# Revit family: UL1008BCELTS1277
name_source: partatom
category: Communication Devices
units: mm (PartAtom-declared; Revit-internal decimal feet)

## family parameters
Cut with Voids When Loaded = No
Host = Face
Maintain Annotation Orientation = No
OmniClass Number = 23.85.80.11.27
OmniClass Title = Lighting Controls
Part Type = Normal
Room Calculation Point = No
Round Connector Dimension = Use Diameter
Shared = Yes

## types (1)
- UL1008BCELTS1277
    Assembly Code = D5090
    Black = Paint - Carbon Black
    Blue = Plastic -Blue
    Default Elevation = 48 "
    Description = The UL1008BCELTS1277 is specifically listed for branch circuit emergency lighting control under the new UL standards. This unit is intended for applications where both a normal and emergency branch circuit are to be connected to the emergency lighting. The UL1008BCELTS1277 automatically transfers from normal to emergency power source upon loss of normal power in the space.The UL1008BCELTS1277 allows emergency lighting to be dimmed with normal lighting during normal times. In the event of a utility power interruption, the UL1008BCELTS1277 will automatically transfer designated emergency fixtures from the dimming control to the emergency power source and bring them to full brightness, regardless of whether the dimming system is in operation or turned off.
    Features = UL1008 listed for transfer of branch circuits
Transfer includes neutral wire
Compatible with all dimming systems
Integral front mounted test swtich
Fire alarm interface option
Safety interlock system prevents cross connection
50A relay contacts allow for high inrush loads
Suitable for flush or surface mounting
    Gray = Paint -  Gray Smooth
    Green = Paint -  Green Textured
    Height = 4.5 "
    Manufacturer = NX Lighting Controls
    Model = UL1008BCELTS1277
    Red = Paint - Red
    Type Comments = Branch Circuit Emergency Lighting Control Transfer Switch
    URL = https://www.currentlighting.com
    Warranty = 5-Years Warranty
    Width = 2.75 "

## geometry (parser evidence)
native form markers: Sweep x2
no freeform markers — native parametric forms only
